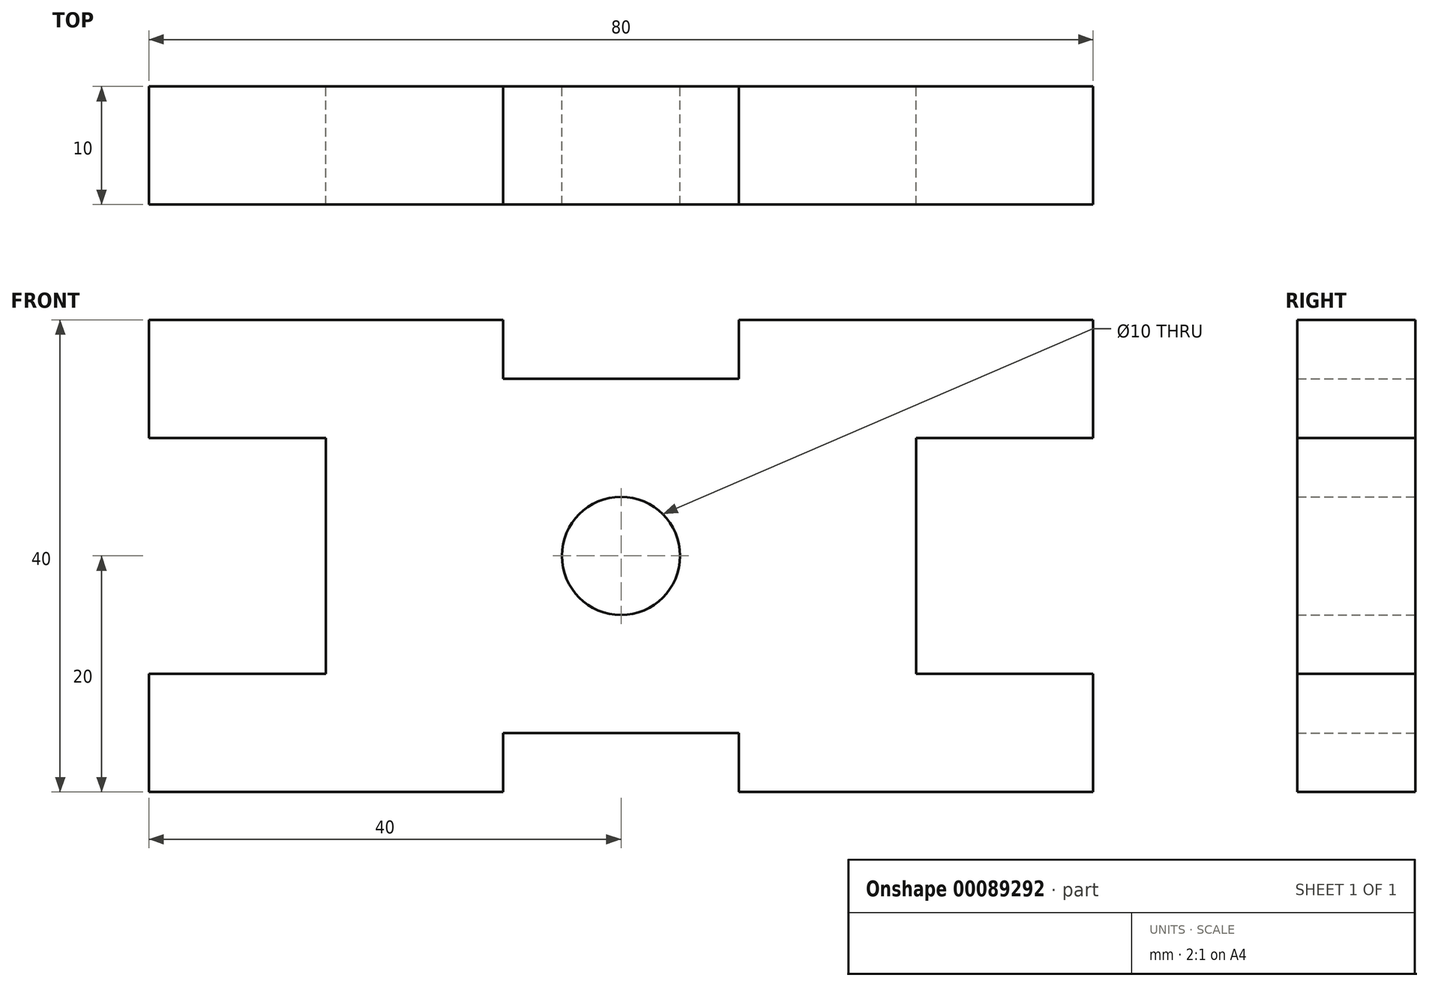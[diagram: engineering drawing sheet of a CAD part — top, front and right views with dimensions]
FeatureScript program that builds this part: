
annotation { "Feature Type Name" : "Feature", "Feature Type Description" : "" }
export const myFeature = defineFeature(function(context is Context, id is Id, definition is map)
    precondition{}
    {
        {
            var Q0;
            Q0=qCreatedBy(makeId("Front.planeOp"),FACE);
            var sketch = newSketch(context, id + "F0", { "sketchPlane" : qUnion([Q0])});
            skCircle(sketch, "E0", {"center": v(0, 0) * mm, "radius": 5 * mm});
            skLineSegment(sketch, "E1.bottom", {"start": v(-40, 20) * mm, "end": v(-10, 20) * mm});
            skLineSegment(sketch, "E1.top", {"start": v(-40, -20) * mm, "end": v(-10, -20) * mm});
            skLineSegment(sketch, "E1.left", {"start": v(-40, 20) * mm, "end": v(-40, 10) * mm});
            skLineSegment(sketch, "E1.right", {"start": v(40, 20) * mm, "end": v(40, 10) * mm});
            skLineSegment(sketch, "E2.bottom", {"start": v(-40, 10) * mm, "end": v(-25, 10) * mm});
            skLineSegment(sketch, "E2.top", {"start": v(-40, -10) * mm, "end": v(-25, -10) * mm});
            skLineSegment(sketch, "E2.right", {"start": v(-25, 10) * mm, "end": v(-25, -10) * mm});
            skLineSegment(sketch, "E3.top", {"start": v(-10, -15) * mm, "end": v(10, -15) * mm});
            skLineSegment(sketch, "E3.left", {"start": v(-10, -20) * mm, "end": v(-10, -15) * mm});
            skLineSegment(sketch, "E3.right", {"start": v(10, -20) * mm, "end": v(10, -15) * mm});
            skLineSegment(sketch, "E4.bottom", {"start": v(40, 10) * mm, "end": v(25, 10) * mm});
            skLineSegment(sketch, "E4.top", {"start": v(40, -10) * mm, "end": v(25, -10) * mm});
            skLineSegment(sketch, "E4.right", {"start": v(25, 10) * mm, "end": v(25, -10) * mm});
            skLineSegment(sketch, "E5.top", {"start": v(-10, 15) * mm, "end": v(10, 15) * mm});
            skLineSegment(sketch, "E5.left", {"start": v(-10, 20) * mm, "end": v(-10, 15) * mm});
            skLineSegment(sketch, "E5.right", {"start": v(10, 20) * mm, "end": v(10, 15) * mm});
            skLineSegment(sketch, "E6.trimOffspring", {"start": v(10, 20) * mm, "end": v(40, 20) * mm});
            skLineSegment(sketch, "E7.trimOffspring", {"start": v(40, -10) * mm, "end": v(40, -20) * mm});
            skLineSegment(sketch, "E8.trimOffspring", {"start": v(10, -20) * mm, "end": v(40, -20) * mm});
            skLineSegment(sketch, "E9.trimOffspring", {"start": v(-40, -10) * mm, "end": v(-40, -20) * mm});
            skLineSegment(sketch, "E10", {"start": v(0, 15) * mm, "end": v(0, -15) * mm, "construction": true});
            skPoint(sketch, "E10.startSnap0", {"position": v(0, 15) * mm});
            skPoint(sketch, "E10.endSnap0", {"position": v(0, -15) * mm});
            skLineSegment(sketch, "E11", {"start": v(0, 0) * mm, "end": v(31.58, 0) * mm, "construction": true});
            skPoint(sketch, "E11.endSnap0", {"position": v(25, 0) * mm});
            skLineSegment(sketch, "E12", {"start": v(0, 0) * mm, "end": v(-32.23, 0) * mm, "construction": true});
            skPoint(sketch, "E12.endSnap0", {"position": v(-25, 0) * mm});
            skSolve(sketch);
        }
        {
            var Q0;
            Q0 = qSketchRegion(id + "F0", true);
            extrude(context, id + "F1", {"entities" : qUnion([Q0]), "depth" : 10 * mm});
        }
    });
